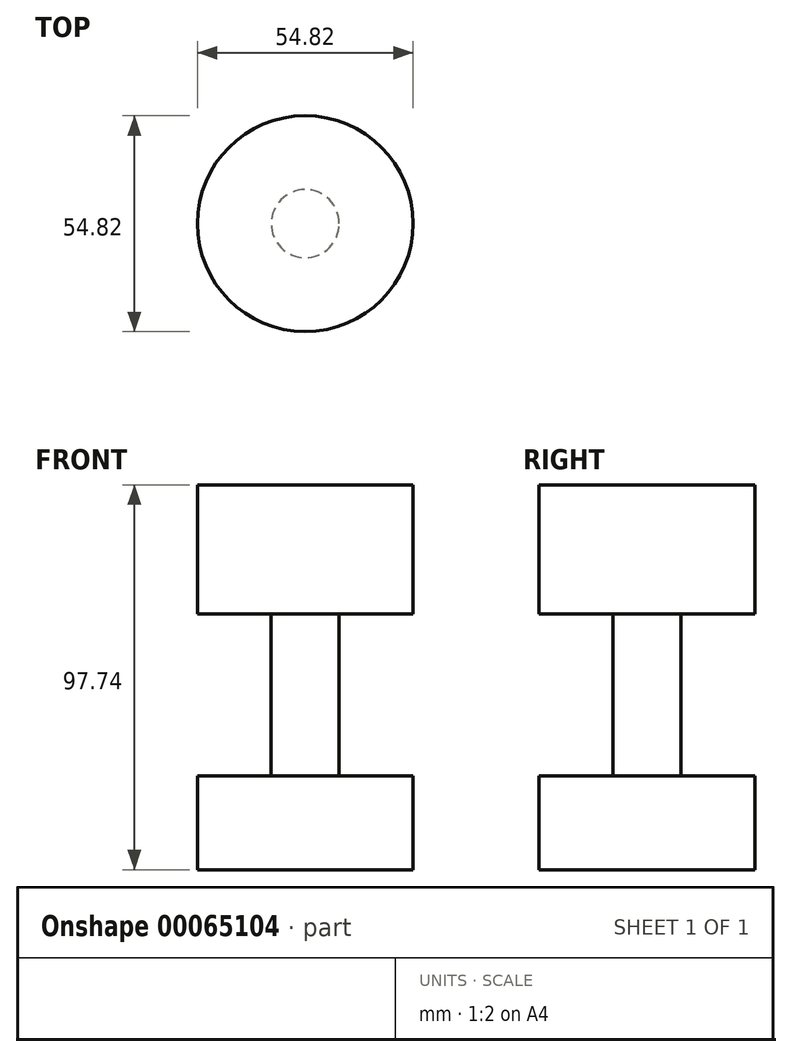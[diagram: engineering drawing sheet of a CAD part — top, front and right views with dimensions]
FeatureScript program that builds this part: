
annotation { "Feature Type Name" : "Feature", "Feature Type Description" : "" }
export const myFeature = defineFeature(function(context is Context, id is Id, definition is map)
    precondition{}
    {
        {
            var Q0;
            Q0=qCreatedBy(makeId("Front.planeOp"),FACE);
            var sketch = newSketch(context, id + "F0", { "sketchPlane" : qUnion([Q0])});
            skLineSegment(sketch, "E0", {"start": v(0, 48.72) * mm, "end": v(-27.41, 48.72) * mm});
            skLineSegment(sketch, "E1", {"start": v(-27.41, 48.72) * mm, "end": v(-27.41, 15.94) * mm});
            skLineSegment(sketch, "E2", {"start": v(-27.41, 15.94) * mm, "end": v(-8.64, 15.94) * mm});
            skLineSegment(sketch, "E3", {"start": v(-8.64, 15.94) * mm, "end": v(-8.64, -25.18) * mm});
            skLineSegment(sketch, "E4", {"start": v(-8.64, -25.18) * mm, "end": v(-27.41, -25.18) * mm});
            skLineSegment(sketch, "E5", {"start": v(-27.41, -25.18) * mm, "end": v(-27.41, -49.02) * mm});
            skLineSegment(sketch, "E6", {"start": v(-27.41, -49.02) * mm, "end": v(0, -49.02) * mm});
            skLineSegment(sketch, "E7", {"start": v(0, -49.02) * mm, "end": v(0, 48.72) * mm});
            skSolve(sketch);
        }
        {
            var Q0;
            Q0 = qSketchRegion(id + "F0", true);
            var Q1;
            Q1=sQuery(id+"F0.wireOp",EDGE,"E7");
            revolve(context, id + "F1", {"entities" : qUnion([Q0]), "axis" : qUnion([Q1]), "revolveType" : RevolveType.FULL});
        }
    });
